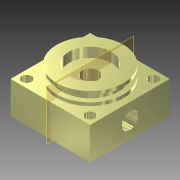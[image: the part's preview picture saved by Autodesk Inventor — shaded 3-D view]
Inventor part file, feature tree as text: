
AUTODESK INVENTOR PART (.ipt)
format: ipt  version: 2011 (Build 150229000, 229)  size: 166,912 bytes
history: native  units: mm
features: sketch x5, hole x4, extrude x1, pattern_linear x1, revolve x1, mirror x1
ambient origin geometry x8: Origin, YZ Plane, XZ Plane, XY Plane, X Axis, Y Axis, Z Axis, Center Point
feature tree (13):
  extrude  "Extrusion1"  Depth=5.0mm
  hole  "Hole1"  [1 undecoded]
  pattern_linear  "Rectangular Pattern1"  Count1=2 Spacing1=39.0mm
  revolve  "Revolution1"  [1 undecoded]
  sketch  "Sketch4"  dims[d17=20.0mm d19=39.0mm d25=8.0mm]
  hole  "Hole2"  [1 undecoded]
  hole  "Hole3"  [1 undecoded]
  hole  "Hole4"  [1 undecoded]
  mirror  "Mirror1"
  sketch  "Sketch1"  dims[d2=20.0mm d3=0.0mm d4=5.0mm]
  sketch  "Sketch2"  dims[d5=39.0mm d6=39.0mm]
  sketch  "Sketch3"  dims[d7=6.0mm d8=6.0mm d9=4.0mm d10=2.0mm d11=90.0deg d12=8.0mm d13=20.594885mm d14=20.0mm d16=39.0mm]
  sketch  "Sketch6"  dims[d26=20.5mm d27=2.0mm d28=4.0mm d29=17.5mm d30=90.0deg d32=6.0mm d33=10.0mm d34=10.0mm d35=10.0mm d36=6.0mm d37=26.0mm d38=6.0mm d39=90.0deg d40=18.0mm d41=0.0mm d42=4.134mm d43=6.0mm d44=26.0mm d45=6.0mm d46=90.0deg d47=18.0mm d48=20.594885mm d49=10.0mm d50=6.0mm d51=26.0mm d52=6.0mm d53=90.0deg d54=10.0mm d55=20.594885mm]
note: 5 required parameter values undecoded (feature->parameter linkage not recoverable at this tier; creation-order binding heuristic only, values carry confidence <= 0.55)